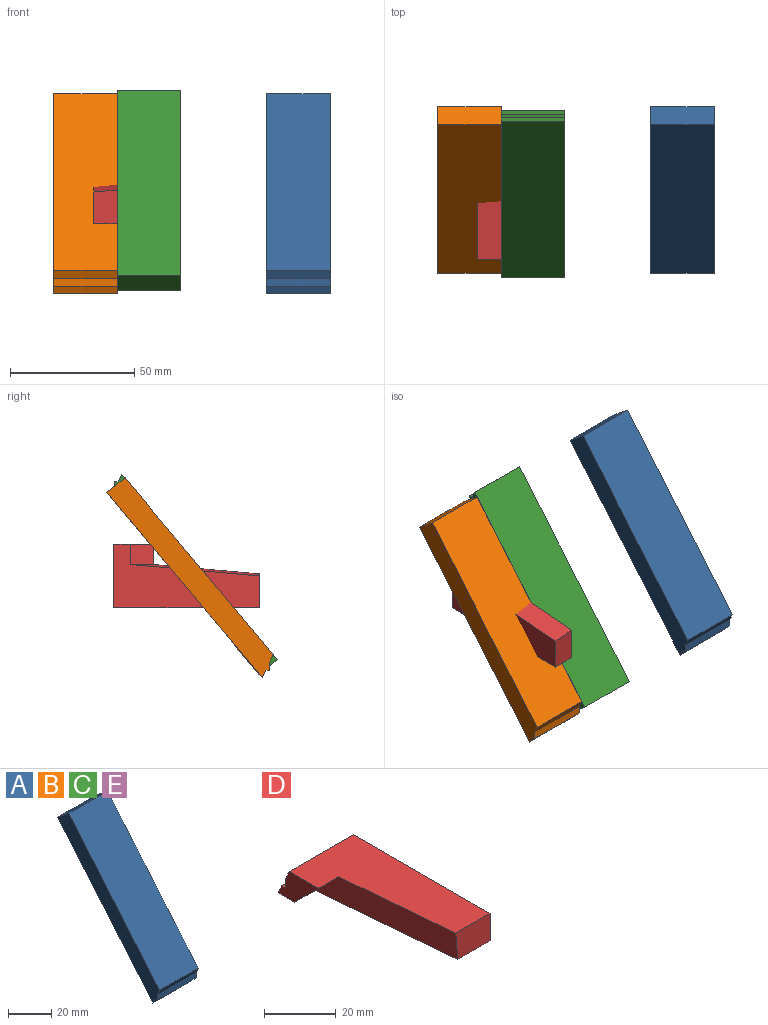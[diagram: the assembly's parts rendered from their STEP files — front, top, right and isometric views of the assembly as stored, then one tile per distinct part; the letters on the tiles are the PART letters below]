
ASSEMBLY  parts=5 mates=2
PART A: 9 faces, bbox 25.4x66.9x80.3 mm
  f0: plane 80.35x66.88mm, normal (1,0,0), area 894.5mm2, adj f2,f3,f4,f5,f6,f7,f8
  f1: plane 80.35x66.88mm, normal (-1,0,0), area 894.5mm2, adj f2,f3,f4,f5,f6,f7,f8
  f2: plane 70.95x59.53mm, normal (0,-0.77,0.64), area 2352.5mm2, adj f0,f1,f4,f5
  f3: plane 74.48x62.5mm, normal (0,0.77,-0.64), area 2469.5mm2, adj f0,f1,f4,f8
  f4: plane 25.4x7.34mm, normal (0,0.62,0.78), area 238.8mm2, adj f0,f1,f2,f3
  f5: plane 25.4x3.08mm, normal (0,-0.91,-0.42), area 86.3mm2, adj f0,f1,f2,f6
  f6: plane 25.4x3.24mm, normal (0,-1,0), area 82.3mm2, adj f0,f1,f5,f7
  f7: plane 25.4x1.51mm, normal (0,0,-1), area 38.4mm2, adj f0,f1,f6,f8
  f8: plane 25.4x3.08mm, normal (0,-0.91,-0.42), area 86.3mm2, adj f0,f1,f3,f7
PART B: same geometry as A
PART C: same geometry as A
PART D: 11 faces, bbox 25.4x58.4x9.4 mm
  f0: plane 13.54x9.4mm, normal (0,-1,0), area 123.3mm2, adj f2,f3,f4,f10
  f1: plane 15.97x9.4mm, normal (-1,0,0), area 82.9mm2, adj f2,f3,f5,f6,f7,f8,f9
  f2: plane 58.43x25.4mm, normal (0,0,-1), area 945.5mm2, adj f0,f1,f4,f8,f9,f10
  f3: plane 54.04x25.4mm, normal (0,0,1), area 949.6mm2, adj f0,f1,f4,f5,f9,f10
  f4: plane 58.43x9.4mm, normal (1,0,0), area 526mm2, adj f0,f2,f3,f5,f6,f7,f8
  f5: plane 25.4x3.08mm, normal (0,0.91,0.42), area 86.3mm2, adj f1,f3,f4,f6
  f6: plane 25.4x3.24mm, normal (0,1,0), area 82.3mm2, adj f1,f4,f5,f7
  f7: plane 25.4x1.51mm, normal (0,0,1), area 38.4mm2, adj f1,f4,f6,f8
  f8: plane 25.4x3.08mm, normal (0,0.91,0.42), area 86.3mm2, adj f1,f2,f4,f7
  f9: plane 9.4x9.4mm, normal (0,-0.71,-0.71), area 107.3mm2, adj f1,f2,f3,f10
  f10: plane 51.85x9.4mm, normal (-0.99,-0.09,-0.09), area 446.6mm2, adj f0,f2,f3,f9
PART E: same geometry as A
PLACE A at identity
PLACE B t=(-85.6,0,0)mm
PLACE C rot(axis=(1,0,0),180deg) t=(-60.2,173.36,81.85)mm
PLACE D rot(axis=(0,1,0),90deg) t=(-69.6,59.66,53.62)mm
PLACE E at identity
MATE revolute D.f3 <-> B.f0  axis (1,0,0) through (-60.2,86.68,40.92)mm
MATE fastened C.f1 <-> B.f0  axis (-1,0,0) through (-60.2,86.68,40.92)mm
